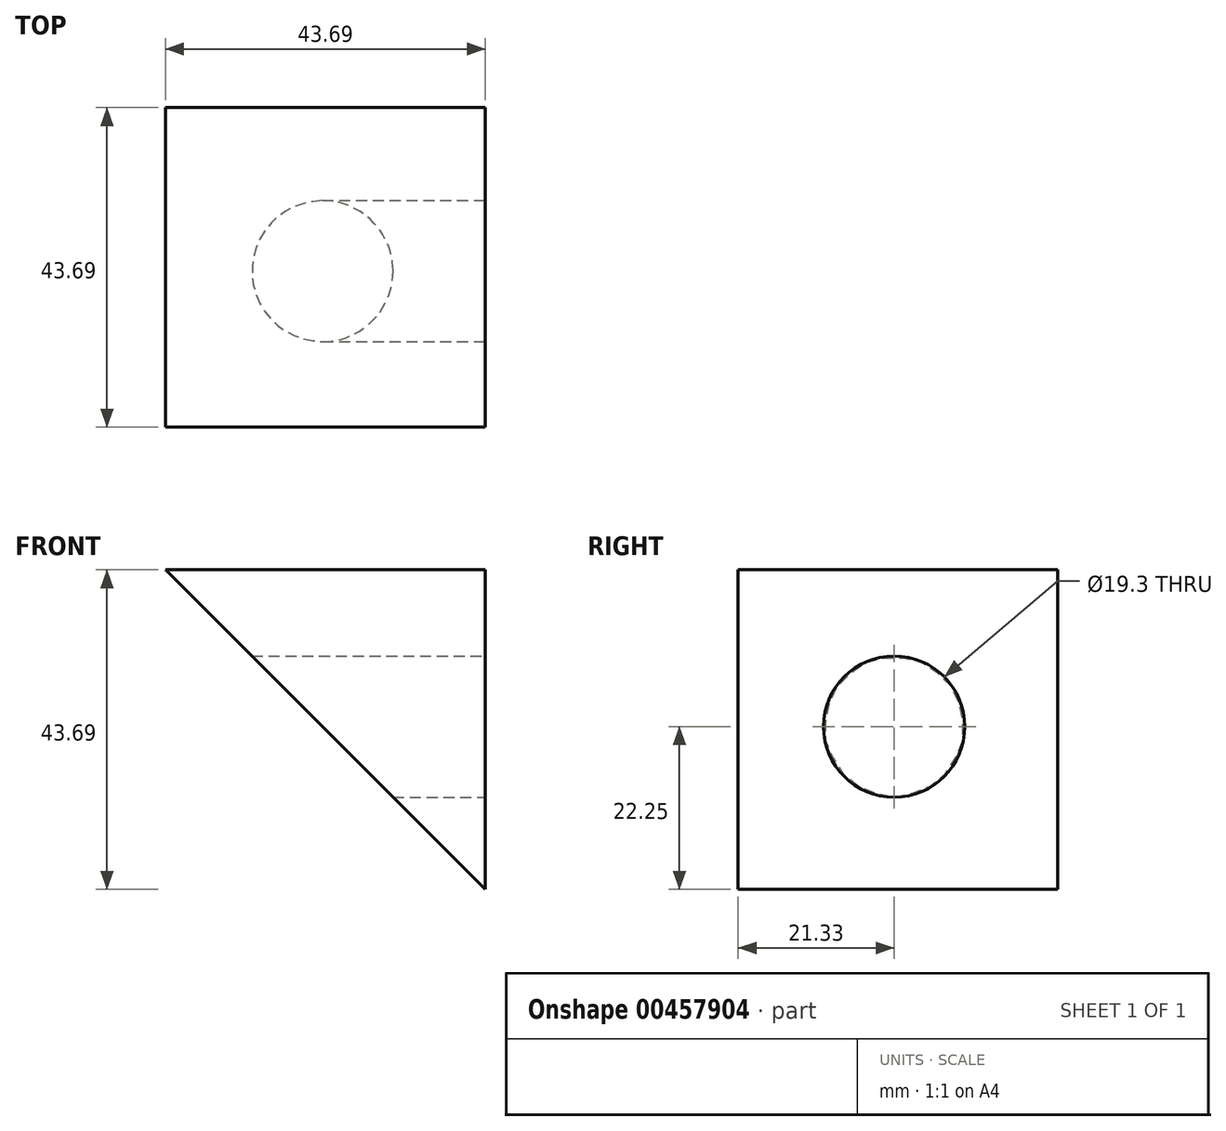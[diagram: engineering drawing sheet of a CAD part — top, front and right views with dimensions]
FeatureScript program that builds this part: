
annotation { "Feature Type Name" : "Feature", "Feature Type Description" : "" }
export const myFeature = defineFeature(function(context is Context, id is Id, definition is map)
    precondition{}
    {
        {
            var Q0;
            Q0=qCreatedBy(makeId("Front.planeOp"),FACE);
            var sketch = newSketch(context, id + "F0", { "sketchPlane" : qUnion([Q0])});
            skPoint(sketch, "E0.0", {"position": v(0, 0) * mm});
            skLineSegment(sketch, "E1.top", {"start": v(0, 43.69) * mm, "end": v(-43.69, 43.69) * mm});
            skLineSegment(sketch, "E1.left", {"start": v(0, 0) * mm, "end": v(0, 43.69) * mm});
            skLineSegment(sketch, "E2", {"start": v(-43.69, 43.69) * mm, "end": v(0, 0) * mm});
            skSolve(sketch);
        }
        {
            var Q0;
            Q0=makeQuery(id+"F0.imprint","IMPRINT",FACE,{"disambiguationData":[TD([[makeQuery(id+"F0.imprint","IMPRINT",EDGE,{"derivedFrom":sQuery(id+"F0.wireOp",EDGE,"E1.top")}),1.0]])]});
            extrude(context, id + "F1", {"entities" : qUnion([Q0]), "depth" : 43.69 * mm});
        }
        {
            var Q0;
            Q0=qCreatedBy(makeId("Right.planeOp"),FACE);
            var sketch = newSketch(context, id + "F2", { "sketchPlane" : qUnion([Q0])});
            skLineSegment(sketch, "E3", {"start": v(-44.72, 0) * mm, "end": v(0, 0) * mm, "construction": true});
            skPoint(sketch, "E4.endSnap0", {"position": v(-22.36, 22.25) * mm});
            skCircle(sketch, "E5", {"center": v(-22.36, 22.25) * mm, "radius": 9.65 * mm});
            skSolve(sketch);
        }
        {
            var Q0;
            Q0 = qSketchRegion(id + "F2", true);
            extrude(context, id + "F3", {"entities" : qUnion([Q0]), "operationType" : NewBodyOperationType.REMOVE, "endBound" : BoundingType.THROUGH_ALL, "oppositeDirection" : true, "depth" : 25.4 * mm});
        }
    });
